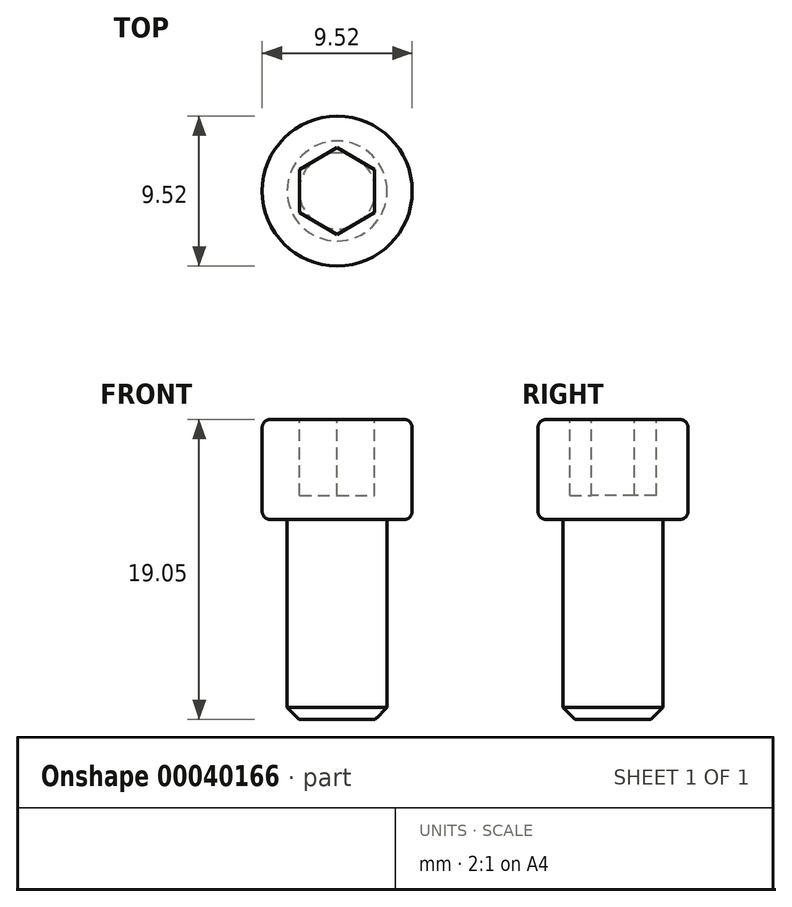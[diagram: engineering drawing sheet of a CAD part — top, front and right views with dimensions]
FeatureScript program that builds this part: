
annotation { "Feature Type Name" : "Feature", "Feature Type Description" : "" }
export const myFeature = defineFeature(function(context is Context, id is Id, definition is map)
    precondition{}
    {
        {
            var Q0;
            Q0=qCreatedBy(makeId("Top.planeOp"),FACE);
            var sketch = newSketch(context, id + "F0", { "sketchPlane" : qUnion([Q0])});
            skCircle(sketch, "E0", {"center": v(0, 0) * mm, "radius": 3.18 * mm});
            skSolve(sketch);
        }
        {
            var Q0;
            Q0=makeQuery(id+"F0.imprint","IMPRINT",FACE,{"disambiguationData":[TD([[makeQuery(id+"F0.imprint","IMPRINT",EDGE,{"derivedFrom":sQuery(id+"F0.wireOp",EDGE,"E0")}),1.0]])]});
            extrude(context, id + "F1", {"entities" : qUnion([Q0]), "oppositeDirection" : true, "depth" : 12.7 * mm});
        }
        {
            var Q0;
            Q0=qCreatedBy(makeId("Top.planeOp"),FACE);
            var sketch = newSketch(context, id + "F2", { "sketchPlane" : qUnion([Q0])});
            skCircle(sketch, "E1", {"center": v(0, 0) * mm, "radius": 4.76 * mm});
            skSolve(sketch);
        }
        {
            var Q0;
            Q0=makeQuery(id+"F2.imprint","IMPRINT",FACE,{"disambiguationData":[TD([[makeQuery(id+"F2.imprint","IMPRINT",EDGE,{"derivedFrom":sQuery(id+"F2.wireOp",EDGE,"E1")}),1.0]])]});
            extrude(context, id + "F3", {"entities" : qUnion([Q0]), "operationType" : NewBodyOperationType.ADD, "depth" : 6.35 * mm});
        }
        {
            var Q0;
            Q0=makeQuery(id+"F3.opExtrude","CAP_FACE",FACE,{"disambiguationData":[OSD([sQuery(id+"F2.wireOp",EDGE,"E1")])],"isStart":false});
            var sketch = newSketch(context, id + "F4", { "sketchPlane" : qUnion([Q0])});
            skCircle(sketch, "E2.cCircle", {"center": v(0, 0) * mm, "radius": 2.38 * mm, "construction": true});
            skLineSegment(sketch, "E2.0", {"start": v(2.38, 1.37) * mm, "end": v(2.38, -1.37) * mm});
            skLineSegment(sketch, "E2.1", {"start": v(2.38, -1.37) * mm, "end": v(0, -2.75) * mm});
            skLineSegment(sketch, "E2.2", {"start": v(0, -2.75) * mm, "end": v(-2.38, -1.37) * mm});
            skLineSegment(sketch, "E2.3", {"start": v(-2.38, -1.37) * mm, "end": v(-2.38, 1.37) * mm});
            skLineSegment(sketch, "E2.4", {"start": v(-2.38, 1.37) * mm, "end": v(0, 2.75) * mm});
            skLineSegment(sketch, "E2.5", {"start": v(0, 2.75) * mm, "end": v(2.38, 1.37) * mm});
            skPoint(sketch, "E2.0.midPoint", {"position": v(2.38, 0) * mm});
            skSolve(sketch);
        }
        {
            var Q0;
            Q0=makeQuery(id+"F4.imprint","IMPRINT",FACE,{"disambiguationData":[TD([[makeQuery(id+"F4.imprint","IMPRINT",EDGE,{"derivedFrom":sQuery(id+"F4.wireOp",EDGE,"E2.0")}),-1.0]])]});
            extrude(context, id + "F5", {"entities" : qUnion([Q0]), "operationType" : NewBodyOperationType.REMOVE, "oppositeDirection" : true, "depth" : 4.83 * mm});
        }
        {
            var Q0;
            Q0=makeQuery(id+"F1.opExtrude","CAP_EDGE",EDGE,{"disambiguationData":[OSD([sQuery(id+"F0.wireOp",EDGE,"E0")])],"isStart":false});
            chamfer(context, id + "F6", {"entities" : qUnion([Q0]), "chamferType" : ChamferType.OFFSET_ANGLE, "width" : 0.76 * mm, "oppositeDirection" : false, "angle" : 45 * degree, "tangentPropagation" : true});
        }
        {
            var Q0;
            Q0=qCreatedBy(makeId("Top.planeOp"),FACE);
            cPlane(context, id + "F7", {"entities" : qUnion([Q0]), "cplaneType" : CPlaneType.OFFSET, "offset" : ((1 / 20) * 2) * mm, "oppositeDirection" : true, "width" : 152.4 * mm, "height" : 152.4 * mm});
        }
        {
            var Q0;
            Q0=qCreatedBy(id+"F7.planeOp",FACE);
            var sketch = newSketch(context, id + "F8", { "sketchPlane" : qUnion([Q0])});
            skCircle(sketch, "E3", {"center": v(0, 0) * mm, "radius": 2.38 * mm});
            skSolve(sketch);
        }
        {
            var Q0;
            Q0=sQuery(id+"F8.wireOp",EDGE,"E3");
            var Q1;
            Q1=makeQuery(id+"F6.opChamfer","BLEND_FACE",FACE,{"disambiguationData":[OSD([sQuery(id+"F0.wireOp",EDGE,"E0")])]});
            extrude(context, id + "F9", {"bodyType" : ToolBodyType.SURFACE, "surfaceEntities" : qUnion([Q0]), "endBound" : BoundingType.UP_TO_SURFACE, "oppositeDirection" : true, "endBoundEntityFace" : qUnion([Q1]), "depth" : 25.4 * mm});
        }
        {
            var Q0;
            Q0=makeQuery(id+"F3.opExtrude","CAP_EDGE",EDGE,{"disambiguationData":[OSD([sQuery(id+"F2.wireOp",EDGE,"E1")])],"isStart":false});
            var Q1;
            Q1=makeQuery(id+"F3.opExtrude","CAP_EDGE",EDGE,{"disambiguationData":[OSD([sQuery(id+"F2.wireOp",EDGE,"E1")])],"isStart":true});
            fillet(context, id + "F10", {"entities" : qUnion([Q0, Q1]), "radius" : 0.5 * mm, "tangentPropagation" : true, "allowEdgeOverflow" : false});
        }
    });
